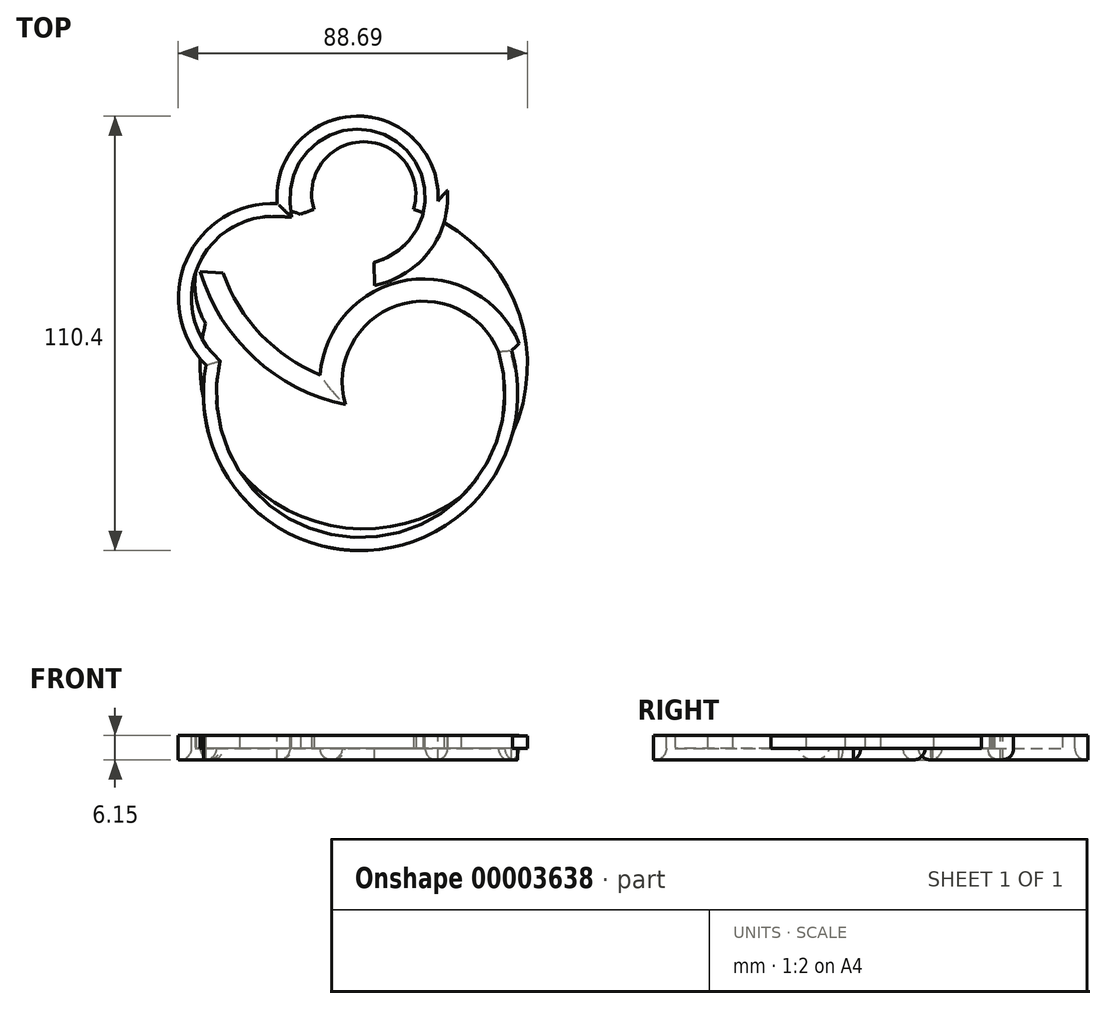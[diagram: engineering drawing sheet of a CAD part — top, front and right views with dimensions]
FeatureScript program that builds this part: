
annotation { "Feature Type Name" : "Feature", "Feature Type Description" : "" }
export const myFeature = defineFeature(function(context is Context, id is Id, definition is map)
    precondition{}
    {
        {
            var Q0;
            Q0=qCreatedBy(makeId("Top.planeOp"),FACE);
            var sketch = newSketch(context, id + "F0", { "sketchPlane" : qUnion([Q0])});
            skArc(sketch, "E0", {"start": v(2.65, 22.8) * mm, "mid": v(37.58, 3.78) * mm, "end": v(25.64, 41.72) * mm});
            skArc(sketch, "E1", {"start": v(42.94, 10.38) * mm, "mid": v(58.06, 37.96) * mm, "end": v(26.66, 39.68) * mm});
            skArc(sketch, "E2", {"start": v(-40.09, 0) * mm, "mid": v(1.13, -47.05) * mm, "end": v(37.58, 3.78) * mm});
            skArc(sketch, "E3", {"start": v(-21.98, 41.1) * mm, "mid": v(-45.07, 26.74) * mm, "end": v(-40.09, 0) * mm});
            skArc(sketch, "E4", {"start": v(2.65, 22.8) * mm, "mid": v(10.64, 59.25) * mm, "end": v(-21.98, 41.1) * mm});
            skArc(sketch, "E5", {"start": v(58.06, 37.96) * mm, "mid": v(39.5, 50.64) * mm, "end": v(18.87, 41.72) * mm});
            skSolve(sketch);
        }
        {
            var Q0;
            Q0=qCreatedBy(makeId("Front.planeOp"),FACE);
            var sketch = newSketch(context, id + "F1", { "sketchPlane" : qUnion([Q0])});
            skCircle(sketch, "E6", {"center": v(38.02, 0) * mm, "radius": 2.92 * mm});
            skSolve(sketch);
        }
        {
            var Q0;
            Q0=makeQuery(id+"F1.imprint","IMPRINT",FACE,{"disambiguationData":[TD([[makeQuery(id+"F1.imprint","IMPRINT",EDGE,{"derivedFrom":sQuery(id+"F1.wireOp",EDGE,"E6")}),1.0]])]});
            var Q1;
            Q1=sQuery(id+"F0.wireOp",EDGE,"E2");
            var Q2;
            Q2=sQuery(id+"F0.wireOp",EDGE,"E2");
            var Q3;
            Q3=sQuery(id+"F0.wireOp",EDGE,"E3");
            var Q4;
            Q4=sQuery(id+"F0.wireOp",EDGE,"E4");
            sweep(context, id + "F2", {"profiles" : qUnion([Q0]), "surfaceProfiles" : qUnion([Q1]), "path" : qUnion([Q2, Q3, Q4])});
        }
        {
            var Q0;
            Q0=qCreatedBy(makeId("Top.planeOp"),FACE);
            var sketch = newSketch(context, id + "F3", { "sketchPlane" : qUnion([Q0])});
            skArc(sketch, "E7", {"start": v(-44.57, 24.01) * mm, "mid": v(-28.08, -1.67) * mm, "end": v(0, -13.63) * mm});
            skArc(sketch, "E8", {"start": v(32.36, 0) * mm, "mid": v(8.25, 12) * mm, "end": v(0, -13.63) * mm});
            skSolve(sketch);
        }
        {
            var Q0;
            Q0=makeQuery(id+"F2.opSweep","CAP_FACE",FACE,{"disambiguationData":[OSD([sQuery(id+"F0.wireOp",VERTEX,"E2.end"),sQuery(id+"F1.wireOp",EDGE,"E6")])],"isStart":true});
            var Q1;
            Q1=sQuery(id+"F3.wireOp",EDGE,"E8");
            var Q2;
            Q2=sQuery(id+"F3.wireOp",EDGE,"E7");
            var Q3;
            Q3=sQuery(id+"F3.wireOp",EDGE,"E8");
            var Q4;
            Q4=sQuery(id+"F3.wireOp",EDGE,"E7");
            sweep(context, id + "F4", {"operationType" : NewBodyOperationType.ADD, "profiles" : qUnion([Q0]), "surfaceProfiles" : qUnion([Q1, Q2]), "path" : qUnion([Q3, Q4])});
        }
        {
            var Q0;
            {var subQ5=sQuery(id+"F0.wireOp",EDGE,"E2");Q0=makeQuery(id+"F0.imprint","IMPRINT",FACE,{"disambiguationData":[TD([[makeQuery(id+"F0.imprint","IMPRINT",EDGE,{"derivedFrom":subQ5}),1.0]])]});}
            var Q1;
            {var subQ1=sQuery(id+"F0.wireOp",EDGE,"E5");Q1=makeQuery(id+"F0.imprint","IMPRINT",FACE,{"disambiguationData":[TD([[makeQuery(id+"F0.imprint","IMPRINT",EDGE,{"derivedFrom":subQ1}),1.0]])]});}
            extrude(context, id + "F5", {"entities" : qUnion([Q0, Q1]), "operationType" : NewBodyOperationType.INTERSECT, "oppositeDirection" : true, "depth" : 8.17 * mm});
        }
        {
            var Q0;
            Q0=makeQuery(id+"F5.boolean.opBoolean","COPY",FACE,{"derivedFrom":makeQuery(id+"F5.opExtrude","CAP_FACE",FACE,{"disambiguationData":[OSD([sQuery(id+"F0.wireOp",EDGE,"E0"),sQuery(id+"F0.wireOp",EDGE,"E1"),sQuery(id+"F0.wireOp",EDGE,"E2"),sQuery(id+"F0.wireOp",EDGE,"E3"),sQuery(id+"F0.wireOp",EDGE,"E4"),sQuery(id+"F0.wireOp",EDGE,"E5")])],"isStart":true})});
            extrude(context, id + "F6", {"entities" : qUnion([Q0]), "operationType" : NewBodyOperationType.ADD, "depth" : 3.23 * mm});
        }
        {
            var Q0;
            Q0=qCreatedBy(makeId("Top.planeOp"),FACE);
            var sketch = newSketch(context, id + "F7", { "sketchPlane" : qUnion([Q0])});
            skCircle(sketch, "E9", {"center": v(0, 0) * mm, "radius": 41.57 * mm});
            skCircle(sketch, "E10", {"center": v(-23.58, 20.5) * mm, "radius": 19.34 * mm});
            skCircle(sketch, "E11", {"center": v(0, 43.55) * mm, "radius": 13.23 * mm});
            skSolve(sketch);
        }
        {
            var Q0;
            {var subQ0=sQuery(id+"F7.wireOp",EDGE,"E10");var subQ1=sQuery(id+"F7.wireOp",EDGE,"E9");var subQ3=makeQuery(id+"F7.imprint","INTERSECT",VERTEX,{"disambiguationData":[OD(0.0)],"derivedFrom":[subQ1,subQ0]});Q0=makeQuery(id+"F7.imprint","IMPRINT",FACE,{"disambiguationData":[TD([[makeQuery(id+"F7.imprint","IMPRINT",EDGE,{"disambiguationData":[TD([[subQ3,-1.0]])],"derivedFrom":subQ1}),-1.0]])]});}
            var Q1;
            {var subQ0=sQuery(id+"F7.wireOp",EDGE,"E10");var subQ1=sQuery(id+"F7.wireOp",EDGE,"E9");var subQ3=makeQuery(id+"F7.imprint","INTERSECT",VERTEX,{"disambiguationData":[OD(0.0)],"derivedFrom":[subQ1,subQ0]});Q1=makeQuery(id+"F7.imprint","IMPRINT",FACE,{"disambiguationData":[TD([[makeQuery(id+"F7.imprint","IMPRINT",EDGE,{"disambiguationData":[TD([[subQ3,-1.0]])],"derivedFrom":subQ1}),1.0]])]});}
            var Q2;
            {var subQ0=sQuery(id+"F7.wireOp",EDGE,"E11");var subQ1=sQuery(id+"F7.wireOp",EDGE,"E9");var subQ3=makeQuery(id+"F7.imprint","INTERSECT",VERTEX,{"disambiguationData":[OD(0.0)],"derivedFrom":[subQ1,subQ0]});Q2=makeQuery(id+"F7.imprint","IMPRINT",FACE,{"disambiguationData":[TD([[makeQuery(id+"F7.imprint","IMPRINT",EDGE,{"disambiguationData":[TD([[subQ3,1.0]])],"derivedFrom":subQ1}),-1.0]])]});}
            var Q3;
            {var subQ0=sQuery(id+"F7.wireOp",EDGE,"E11");var subQ1=sQuery(id+"F7.wireOp",EDGE,"E9");var subQ3=makeQuery(id+"F7.imprint","INTERSECT",VERTEX,{"disambiguationData":[OD(0.0)],"derivedFrom":[subQ1,subQ0]});Q3=makeQuery(id+"F7.imprint","IMPRINT",FACE,{"disambiguationData":[TD([[makeQuery(id+"F7.imprint","IMPRINT",EDGE,{"disambiguationData":[TD([[subQ3,-1.0]])],"derivedFrom":subQ1}),1.0]])]});}
            var Q4;
            {var subQ0=sQuery(id+"F7.wireOp",EDGE,"E11");var subQ1=sQuery(id+"F7.wireOp",EDGE,"E9");var subQ3=makeQuery(id+"F7.imprint","INTERSECT",VERTEX,{"disambiguationData":[OD(0.0)],"derivedFrom":[subQ1,subQ0]});Q4=makeQuery(id+"F7.imprint","IMPRINT",FACE,{"disambiguationData":[TD([[makeQuery(id+"F7.imprint","IMPRINT",EDGE,{"disambiguationData":[TD([[subQ3,1.0]])],"derivedFrom":subQ1}),1.0]])]});}
            extrude(context, id + "F8", {"entities" : qUnion([Q0, Q1, Q2, Q3, Q4]), "operationType" : NewBodyOperationType.ADD, "depth" : 3.17 * mm});
        }
    });
